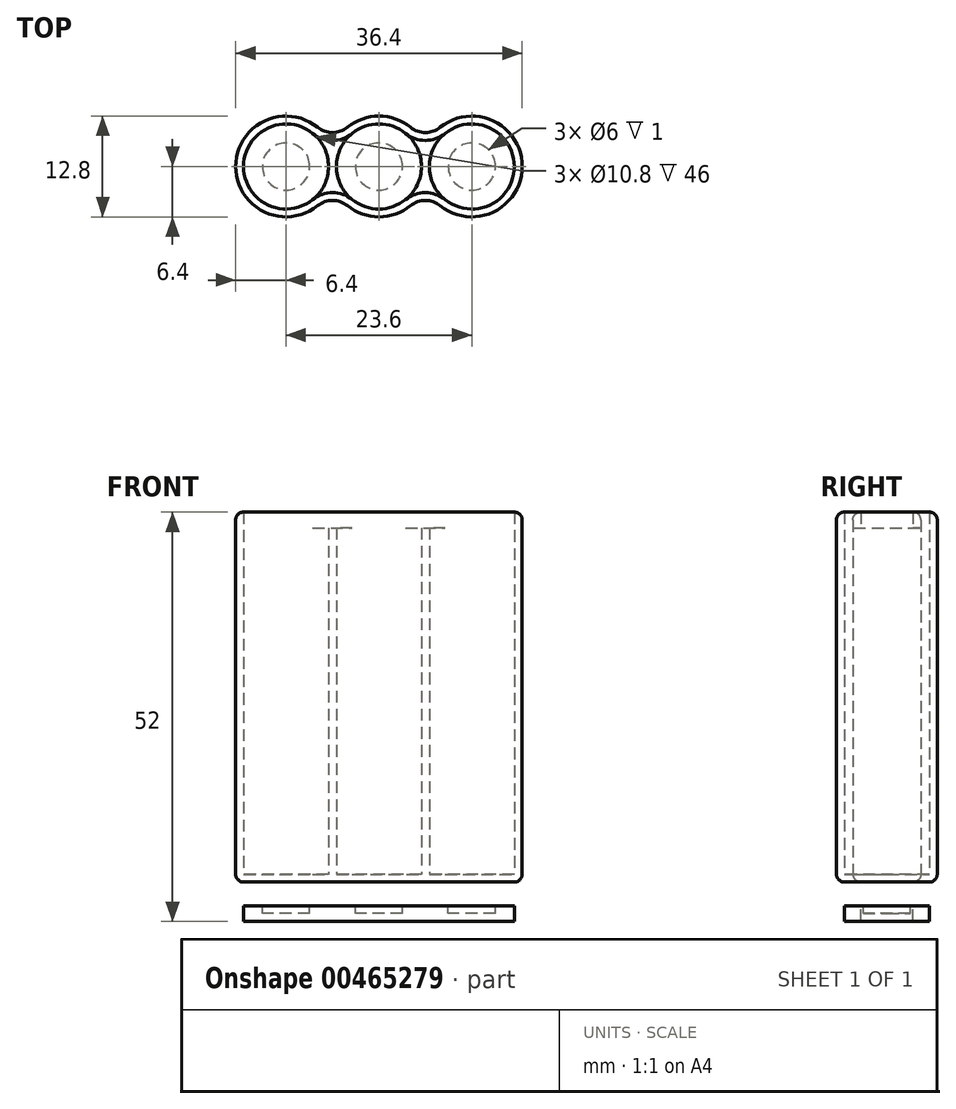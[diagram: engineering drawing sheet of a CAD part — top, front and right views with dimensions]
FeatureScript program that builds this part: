
annotation { "Feature Type Name" : "Feature", "Feature Type Description" : "" }
export const myFeature = defineFeature(function(context is Context, id is Id, definition is map)
    precondition{}
    {
        {
            var Q0;
            Q0=qCreatedBy(makeId("Top.planeOp"),FACE);
            var sketch = newSketch(context, id + "F0", { "sketchPlane" : qUnion([Q0])});
            skCircle(sketch, "E0", {"center": v(0, 0) * mm, "radius": 5.4 * mm});
            skCircle(sketch, "E1.1.0.0", {"center": v(11.8, 0) * mm, "radius": 5.4 * mm});
            skCircle(sketch, "E1.2.0.0", {"center": v(23.6, 0) * mm, "radius": 5.4 * mm});
            skLineSegment(sketch, "E1.direction1", {"start": v(0, 0) * mm, "end": v(11.8, 0) * mm, "construction": true});
            skArc(sketch, "E2.0", {"start": v(7.78, -4.98) * mm, "mid": v(11.8, -6.4) * mm, "end": v(15.82, -4.98) * mm});
            skArc(sketch, "E3.0", {"start": v(19.58, -4.98) * mm, "mid": v(30, 0) * mm, "end": v(19.58, 4.98) * mm});
            skArc(sketch, "E4.0", {"start": v(4.02, 4.98) * mm, "mid": v(-6.4, 0) * mm, "end": v(4.02, -4.98) * mm});
            skArc(sketch, "E5.trimOffspring", {"start": v(15.82, 4.98) * mm, "mid": v(11.8, 6.4) * mm, "end": v(7.78, 4.98) * mm});
            skPoint(sketch, "E6.visualSharp", {"position": v(5.9, 2.48) * mm});
            skArc(sketch, "E6.filletArc", {"start": v(4.02, 4.98) * mm, "mid": v(5.9, 4.32) * mm, "end": v(7.78, 4.98) * mm});
            skPoint(sketch, "E7.visualSharp", {"position": v(17.7, 2.48) * mm});
            skArc(sketch, "E7.filletArc", {"start": v(15.82, 4.98) * mm, "mid": v(17.7, 4.32) * mm, "end": v(19.58, 4.98) * mm});
            skPoint(sketch, "E8.visualSharp", {"position": v(17.7, -2.48) * mm});
            skArc(sketch, "E8.filletArc", {"start": v(19.58, -4.98) * mm, "mid": v(17.7, -4.32) * mm, "end": v(15.82, -4.98) * mm});
            skPoint(sketch, "E9.visualSharp", {"position": v(5.9, -2.48) * mm});
            skArc(sketch, "E9.filletArc", {"start": v(7.78, -4.98) * mm, "mid": v(5.9, -4.32) * mm, "end": v(4.02, -4.98) * mm});
            skArc(sketch, "E10.0", {"start": v(3.39, 4.2) * mm, "mid": v(5.9, 3.32) * mm, "end": v(8.41, 4.2) * mm});
            skArc(sketch, "E11.0", {"start": v(15.19, 4.2) * mm, "mid": v(17.7, 3.32) * mm, "end": v(20.21, 4.2) * mm});
            skArc(sketch, "E12.0", {"start": v(20.21, -4.2) * mm, "mid": v(17.7, -3.32) * mm, "end": v(15.19, -4.2) * mm});
            skArc(sketch, "E13.0", {"start": v(8.41, -4.2) * mm, "mid": v(5.9, -3.32) * mm, "end": v(3.39, -4.2) * mm});
            skSolve(sketch);
        }
        {
            var Q0;
            Q0=makeQuery(id+"F0.imprint","IMPRINT",FACE,{"disambiguationData":[TD([[makeQuery(id+"F0.imprint","IMPRINT",EDGE,{"derivedFrom":sQuery(id+"F0.wireOp",EDGE,"E2.0")}),1.0]])]});
            extrude(context, id + "F1", {"entities" : qUnion([Q0]), "depth" : 47 * mm});
        }
        {
            var Q0;
            {var subQ0=sQuery(id+"F0.wireOp",EDGE,"E10.0");Q0=makeQuery(id+"F0.imprint","IMPRINT",FACE,{"disambiguationData":[TD([[makeQuery(id+"F0.imprint","IMPRINT",EDGE,{"derivedFrom":subQ0}),-1.0]])]});}
            var Q1;
            {var subQ0=sQuery(id+"F0.wireOp",EDGE,"E11.0");Q1=makeQuery(id+"F0.imprint","IMPRINT",FACE,{"disambiguationData":[TD([[makeQuery(id+"F0.imprint","IMPRINT",EDGE,{"derivedFrom":subQ0}),-1.0]])]});}
            extrude(context, id + "F2", {"entities" : qUnion([Q0, Q1]), "operationType" : NewBodyOperationType.ADD, "depth" : 45 * mm});
        }
        {
            var Q0;
            {var subQ0=sQuery(id+"F0.wireOp",EDGE,"E0");var subQ1=makeQuery(id+"F0.imprint","INTERSECT",VERTEX,{"derivedFrom":[subQ0,sQuery(id+"F0.wireOp",EDGE,"E10.0")]});Q0=makeQuery(id+"F0.imprint","IMPRINT",FACE,{"disambiguationData":[TD([[makeQuery(id+"F0.imprint","IMPRINT",EDGE,{"disambiguationData":[TD([[subQ1,-1.0]])],"derivedFrom":subQ0}),1.0]])]});}
            var Q1;
            {var subQ0=sQuery(id+"F0.wireOp",EDGE,"E1.1.0.0");var subQ1=makeQuery(id+"F0.imprint","INTERSECT",VERTEX,{"derivedFrom":[subQ0,sQuery(id+"F0.wireOp",EDGE,"E10.0")]});Q1=makeQuery(id+"F0.imprint","IMPRINT",FACE,{"disambiguationData":[TD([[makeQuery(id+"F0.imprint","IMPRINT",EDGE,{"disambiguationData":[TD([[subQ1,1.0]])],"derivedFrom":subQ0}),1.0]])]});}
            var Q2;
            {var subQ0=sQuery(id+"F0.wireOp",EDGE,"E1.2.0.0");var subQ1=makeQuery(id+"F0.imprint","INTERSECT",VERTEX,{"derivedFrom":[subQ0,sQuery(id+"F0.wireOp",EDGE,"E11.0")]});Q2=makeQuery(id+"F0.imprint","IMPRINT",FACE,{"disambiguationData":[TD([[makeQuery(id+"F0.imprint","IMPRINT",EDGE,{"disambiguationData":[TD([[subQ1,-1.0]])],"derivedFrom":subQ0}),1.0]])]});}
            extrude(context, id + "F3", {"entities" : qUnion([Q0, Q1, Q2]), "operationType" : NewBodyOperationType.ADD, "depth" : 1 * mm});
        }
        {
            var Q0;
            Q0=makeQuery(id+"F1.opExtrude","CAP_EDGE",EDGE,{"disambiguationData":[OSD([sQuery(id+"F0.wireOp",EDGE,"E5.trimOffspring")])],"isStart":false});
            var Q1;
            Q1=makeQuery(id+"F1.opExtrude","CAP_EDGE",EDGE,{"disambiguationData":[OSD([sQuery(id+"F0.wireOp",EDGE,"E6.filletArc")])],"isStart":false});
            var Q2;
            Q2=makeQuery(id+"F1.opExtrude","CAP_EDGE",EDGE,{"disambiguationData":[OSD([sQuery(id+"F0.wireOp",EDGE,"E4.0")])],"isStart":false});
            var Q3;
            Q3=makeQuery(id+"F1.opExtrude","CAP_EDGE",EDGE,{"disambiguationData":[OSD([sQuery(id+"F0.wireOp",EDGE,"E9.filletArc")])],"isStart":false});
            var Q4;
            Q4=makeQuery(id+"F1.opExtrude","CAP_EDGE",EDGE,{"disambiguationData":[OSD([sQuery(id+"F0.wireOp",EDGE,"E2.0")])],"isStart":false});
            var Q5;
            Q5=makeQuery(id+"F1.opExtrude","CAP_EDGE",EDGE,{"disambiguationData":[OSD([sQuery(id+"F0.wireOp",EDGE,"E8.filletArc")])],"isStart":false});
            var Q6;
            Q6=makeQuery(id+"F1.opExtrude","CAP_EDGE",EDGE,{"disambiguationData":[OSD([sQuery(id+"F0.wireOp",EDGE,"E3.0")])],"isStart":false});
            var Q7;
            Q7=makeQuery(id+"F1.opExtrude","CAP_EDGE",EDGE,{"disambiguationData":[OSD([sQuery(id+"F0.wireOp",EDGE,"E7.filletArc")])],"isStart":false});
            var Q8;
            {var subQ0=sQuery(id+"F0.wireOp",EDGE,"E1.2.0.0");var subQ1=sQuery(id+"F0.wireOp",EDGE,"E1.1.0.0");var subQ2=sQuery(id+"F0.wireOp",EDGE,"E0");var subQ3=sQuery(id+"F0.wireOp",EDGE,"E12.0");var subQ4=sQuery(id+"F0.wireOp",EDGE,"E11.0");var subQ5=sQuery(id+"F0.wireOp",EDGE,"E13.0");var subQ6=sQuery(id+"F0.wireOp",EDGE,"E10.0");Q8=makeQuery(id+"F3.boolean.opBoolean","MERGE",FACE,{"derivedFrom":[makeQuery(id+"F2.boolean.opBoolean","MERGE",FACE,{"derivedFrom":[makeQuery(id+"F1.opExtrude","CAP_FACE",FACE,{"disambiguationData":[OSD([subQ2,subQ1,subQ0,sQuery(id+"F0.wireOp",EDGE,"E2.0"),sQuery(id+"F0.wireOp",EDGE,"E3.0"),sQuery(id+"F0.wireOp",EDGE,"E4.0"),sQuery(id+"F0.wireOp",EDGE,"E5.trimOffspring"),sQuery(id+"F0.wireOp",EDGE,"E6.filletArc"),sQuery(id+"F0.wireOp",EDGE,"E7.filletArc"),sQuery(id+"F0.wireOp",EDGE,"E8.filletArc"),sQuery(id+"F0.wireOp",EDGE,"E9.filletArc"),subQ6,subQ4,subQ3,subQ5])],"isStart":true}),makeQuery(id+"F2.opExtrude","CAP_FACE",FACE,{"disambiguationData":[OSD([subQ2,subQ1,subQ6,subQ5])],"isStart":true}),makeQuery(id+"F2.opExtrude","CAP_FACE",FACE,{"disambiguationData":[OSD([subQ1,subQ0,subQ4,subQ3])],"isStart":true})]}),makeQuery(id+"F3.opExtrude","CAP_FACE",FACE,{"disambiguationData":[OSD([subQ2])],"isStart":true}),makeQuery(id+"F3.opExtrude","CAP_FACE",FACE,{"disambiguationData":[OSD([subQ1])],"isStart":true}),makeQuery(id+"F3.opExtrude","CAP_FACE",FACE,{"disambiguationData":[OSD([subQ0])],"isStart":true})]});}
            fillet(context, id + "F4", {"entities" : qUnion([Q0, Q1, Q2, Q3, Q4, Q5, Q6, Q7, Q8]), "radius" : 1 * mm, "tangentPropagation" : true, "allowEdgeOverflow" : false});
        }
        {
            var Q0;
            {var subQ0=sQuery(id+"F0.wireOp",EDGE,"E0");var subQ1=makeQuery(id+"F0.imprint","INTERSECT",VERTEX,{"derivedFrom":[subQ0,sQuery(id+"F0.wireOp",EDGE,"E10.0")]});Q0=makeQuery(id+"F0.imprint","IMPRINT",FACE,{"disambiguationData":[TD([[makeQuery(id+"F0.imprint","IMPRINT",EDGE,{"disambiguationData":[TD([[subQ1,-1.0]])],"derivedFrom":subQ0}),1.0]])]});}
            var Q1;
            {var subQ0=sQuery(id+"F0.wireOp",EDGE,"E10.0");Q1=makeQuery(id+"F0.imprint","IMPRINT",FACE,{"disambiguationData":[TD([[makeQuery(id+"F0.imprint","IMPRINT",EDGE,{"derivedFrom":subQ0}),-1.0]])]});}
            var Q2;
            {var subQ0=sQuery(id+"F0.wireOp",EDGE,"E1.1.0.0");var subQ1=makeQuery(id+"F0.imprint","INTERSECT",VERTEX,{"derivedFrom":[subQ0,sQuery(id+"F0.wireOp",EDGE,"E10.0")]});Q2=makeQuery(id+"F0.imprint","IMPRINT",FACE,{"disambiguationData":[TD([[makeQuery(id+"F0.imprint","IMPRINT",EDGE,{"disambiguationData":[TD([[subQ1,1.0]])],"derivedFrom":subQ0}),1.0]])]});}
            var Q3;
            {var subQ0=sQuery(id+"F0.wireOp",EDGE,"E11.0");Q3=makeQuery(id+"F0.imprint","IMPRINT",FACE,{"disambiguationData":[TD([[makeQuery(id+"F0.imprint","IMPRINT",EDGE,{"derivedFrom":subQ0}),-1.0]])]});}
            var Q4;
            {var subQ0=sQuery(id+"F0.wireOp",EDGE,"E1.2.0.0");var subQ1=makeQuery(id+"F0.imprint","INTERSECT",VERTEX,{"derivedFrom":[subQ0,sQuery(id+"F0.wireOp",EDGE,"E11.0")]});Q4=makeQuery(id+"F0.imprint","IMPRINT",FACE,{"disambiguationData":[TD([[makeQuery(id+"F0.imprint","IMPRINT",EDGE,{"disambiguationData":[TD([[subQ1,-1.0]])],"derivedFrom":subQ0}),1.0]])]});}
            extrude(context, id + "F5", {"entities" : qUnion([Q0, Q1, Q2, Q3, Q4]), "oppositeDirection" : true, "depth" : 5 * mm, "hasSecondDirection" : true, "secondDirectionOppositeDirection" : true, "secondDirectionDepth" : 3 * mm});
        }
        {
            var Q0;
            Q0=makeQuery(id+"F5.opExtrude","CAP_FACE",FACE,{"disambiguationData":[OSD([sQuery(id+"F0.wireOp",EDGE,"E0"),sQuery(id+"F0.wireOp",EDGE,"E1.1.0.0"),sQuery(id+"F0.wireOp",EDGE,"E1.2.0.0"),sQuery(id+"F0.wireOp",EDGE,"E10.0"),sQuery(id+"F0.wireOp",EDGE,"E11.0"),sQuery(id+"F0.wireOp",EDGE,"E12.0"),sQuery(id+"F0.wireOp",EDGE,"E13.0")])],"isStart":true});
            var sketch = newSketch(context, id + "F6", { "sketchPlane" : qUnion([Q0])});
            skCircle(sketch, "E14", {"center": v(0, 0) * mm, "radius": 3 * mm});
            skCircle(sketch, "E15", {"center": v(11.8, 0) * mm, "radius": 3 * mm});
            skCircle(sketch, "E16", {"center": v(23.6, 0) * mm, "radius": 3 * mm});
            skSolve(sketch);
        }
        {
            var Q0;
            Q0=makeQuery(id+"F6.imprint","IMPRINT",FACE,{"disambiguationData":[TD([[makeQuery(id+"F6.imprint","IMPRINT",EDGE,{"derivedFrom":sQuery(id+"F6.wireOp",EDGE,"E14")}),1.0]])]});
            var Q1;
            Q1=makeQuery(id+"F6.imprint","IMPRINT",FACE,{"disambiguationData":[TD([[makeQuery(id+"F6.imprint","IMPRINT",EDGE,{"derivedFrom":sQuery(id+"F6.wireOp",EDGE,"E15")}),1.0]])]});
            var Q2;
            Q2=makeQuery(id+"F6.imprint","IMPRINT",FACE,{"disambiguationData":[TD([[makeQuery(id+"F6.imprint","IMPRINT",EDGE,{"derivedFrom":sQuery(id+"F6.wireOp",EDGE,"E16")}),1.0]])]});
            extrude(context, id + "F7", {"entities" : qUnion([Q0, Q1, Q2]), "operationType" : NewBodyOperationType.REMOVE, "oppositeDirection" : true, "depth" : 1 * mm});
        }
    });
